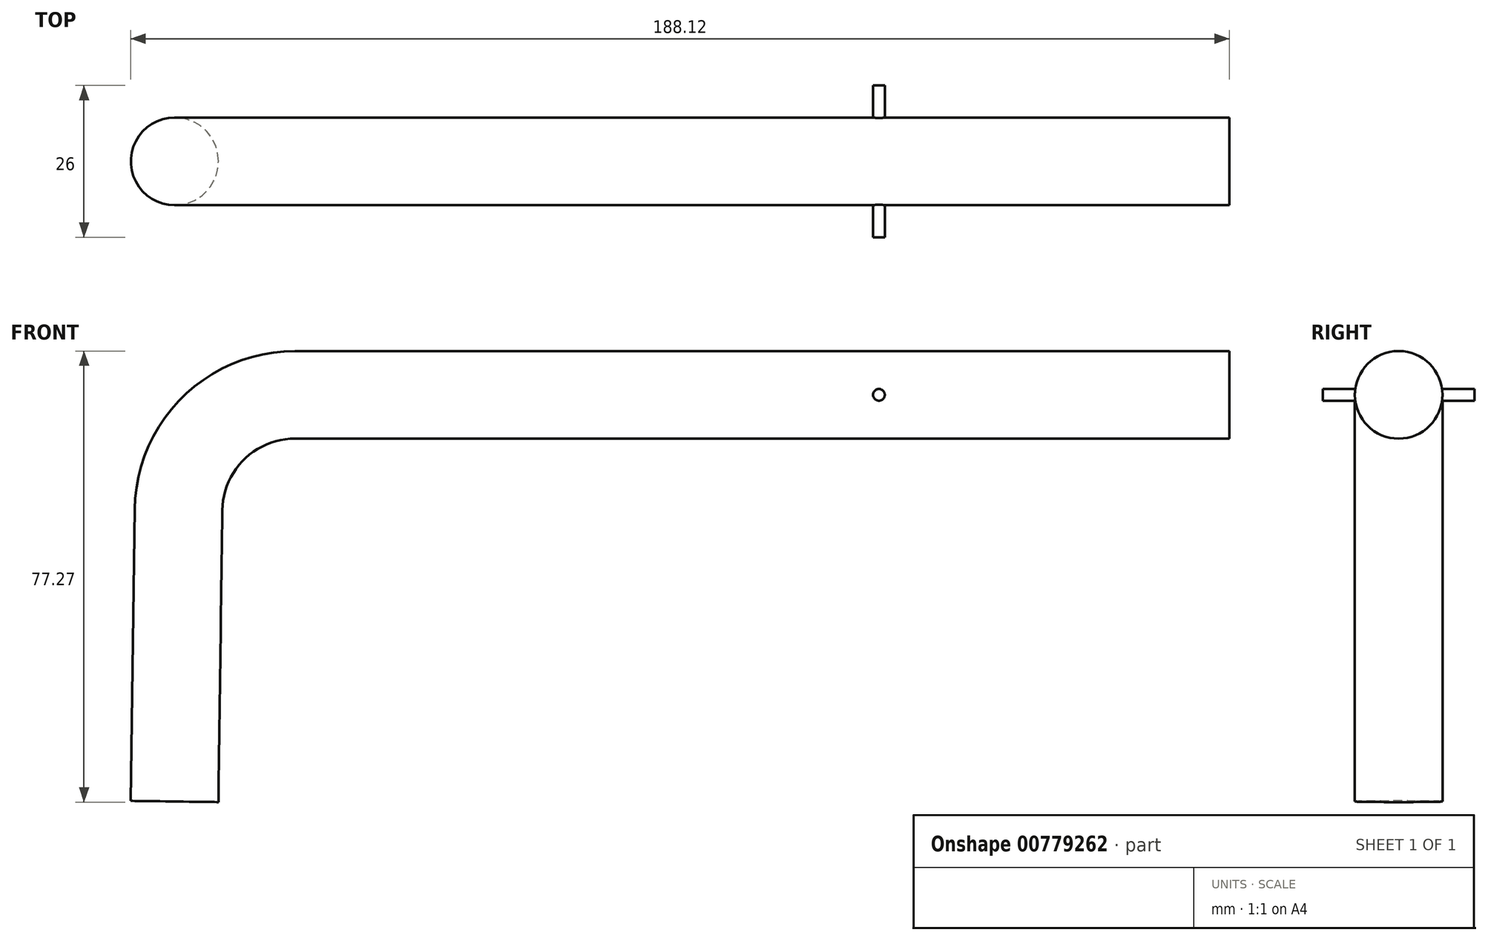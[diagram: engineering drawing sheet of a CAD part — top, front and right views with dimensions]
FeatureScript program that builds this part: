
annotation { "Feature Type Name" : "Feature", "Feature Type Description" : "" }
export const myFeature = defineFeature(function(context is Context, id is Id, definition is map)
    precondition{}
    {
        {
            var Q0;
            Q0=qCreatedBy(makeId("Right.planeOp"),FACE);
            var sketch = newSketch(context, id + "F0", { "sketchPlane" : qUnion([Q0])});
            skCircle(sketch, "E0", {"center": v(0, 0) * mm, "radius": 7.5 * mm});
            skSolve(sketch);
        }
        {
            var Q0;
            Q0=qCreatedBy(makeId("Front.planeOp"),FACE);
            var sketch = newSketch(context, id + "F1", { "sketchPlane" : qUnion([Q0])});
            skLineSegment(sketch, "E1", {"start": v(0, 0) * mm, "end": v(-160, 0) * mm});
            skArc(sketch, "E2", {"start": v(-160, 0) * mm, "mid": v(-174, -5.75) * mm, "end": v(-179.94, -19.67) * mm});
            skLineSegment(sketch, "E3", {"start": v(-179.94, -19.67) * mm, "end": v(-180.62, -69.67) * mm});
            skSolve(sketch);
        }
        {
            var Q0;
            Q0=makeQuery(id+"F0.imprint","IMPRINT",FACE,{"disambiguationData":[TD([[makeQuery(id+"F0.imprint","IMPRINT",EDGE,{"derivedFrom":sQuery(id+"F0.wireOp",EDGE,"E0")}),1.0]])]});
            var Q1;
            Q1=sQuery(id+"F1.wireOp",EDGE,"E1");
            var Q2;
            Q2=sQuery(id+"F1.wireOp",EDGE,"4812c1e0-19b3-4721-98a4-b00b586b1ae6");
            var Q3;
            Q3=sQuery(id+"F1.wireOp",EDGE,"TqZZd5vu-T1Av-oWCC-3y6h-iHtPcbeUtyxu");
            var Q4;
            Q4=sQuery(id+"F1.wireOp",EDGE,"E2");
            var Q5;
            Q5=sQuery(id+"F1.wireOp",EDGE,"E3");
            sweep(context, id + "F2", {"profiles" : qUnion([Q0]), "path" : qUnion([Q1, Q2, Q3, Q4, Q5])});
        }
        {
            var Q0;
            Q0=qCreatedBy(makeId("Front.planeOp"),FACE);
            var sketch = newSketch(context, id + "F3", { "sketchPlane" : qUnion([Q0])});
            skCircle(sketch, "E4", {"center": v(-60, 0) * mm, "radius": 1 * mm});
            skSolve(sketch);
        }
        {
            var Q0;
            Q0=qSketchRegion(id+"F3",true);
            extrude(context, id + "F4", {"entities" : qUnion([Q0]), "operationType" : NewBodyOperationType.ADD, "depth" : 13 * mm});
        }
        {
            var Q0;
            Q0=makeQuery(id+"F4.opExtrude","CAP_FACE",FACE,{"disambiguationData":[OSD([sQuery(id+"F3.wireOp",EDGE,"E4")])],"isStart":false});
            extrude(context, id + "F5", {"entities" : qUnion([Q0]), "operationType" : NewBodyOperationType.ADD, "oppositeDirection" : true, "depth" : 26 * mm});
        }
    });
